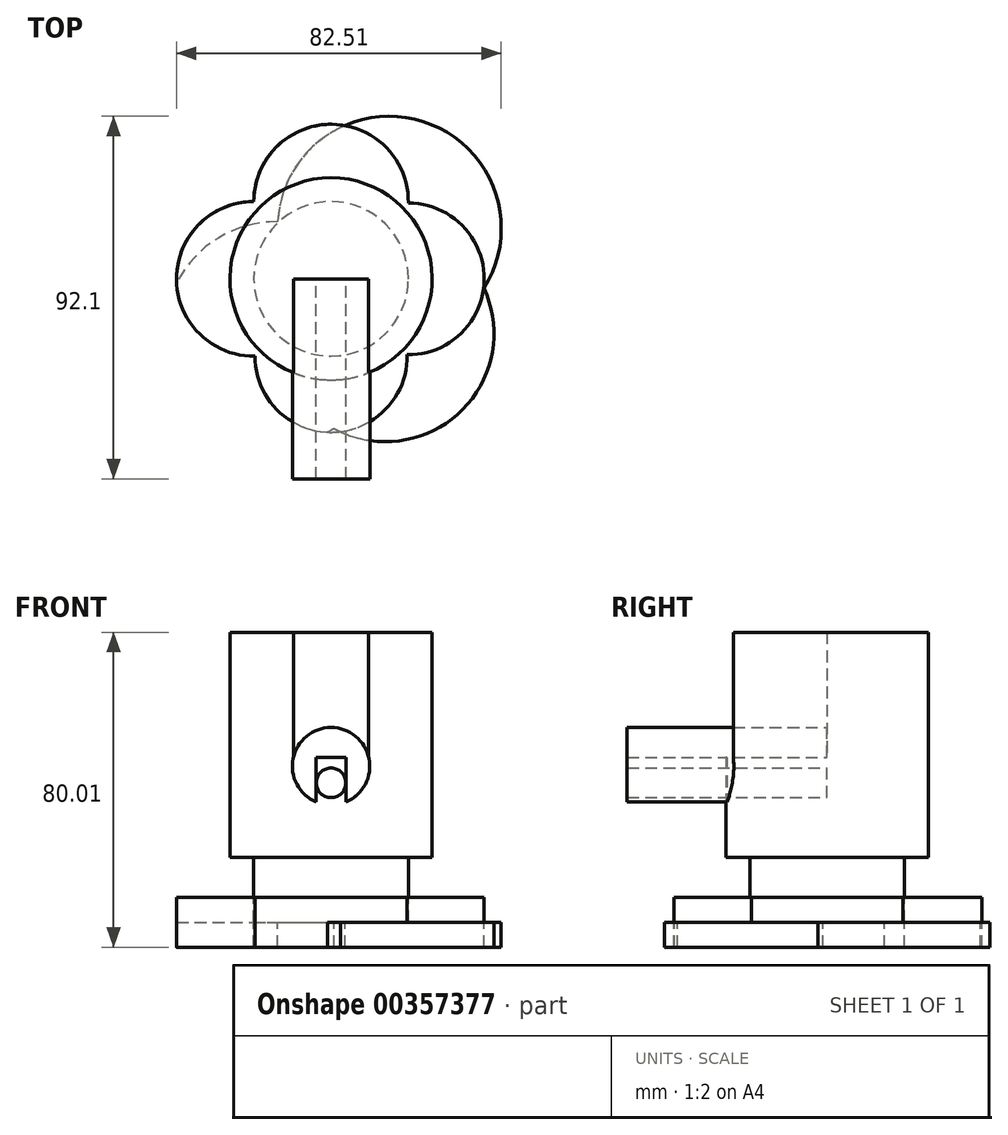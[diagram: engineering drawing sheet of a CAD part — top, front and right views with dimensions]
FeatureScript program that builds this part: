
annotation { "Feature Type Name" : "Feature", "Feature Type Description" : "" }
export const myFeature = defineFeature(function(context is Context, id is Id, definition is map)
    precondition{}
    {
        {
            var Q0;
            Q0=qCreatedBy(makeId("Top.planeOp"),FACE);
            var sketch = newSketch(context, id + "F0", { "sketchPlane" : qUnion([Q0])});
            skCircle(sketch, "E0", {"center": v(0, 0) * mm, "radius": 25.68 * mm});
            skSolve(sketch);
        }
        {
            var Q0;
            Q0=makeQuery(id+"F0.imprint","IMPRINT",FACE,{"disambiguationData":[TD([[makeQuery(id+"F0.imprint","IMPRINT",EDGE,{"derivedFrom":sQuery(id+"F0.wireOp",EDGE,"E0")}),1.0]])]});
            extrude(context, id + "F1", {"entities" : qUnion([Q0]), "depth" : 25.4 * mm, "offsetDistance" : 25.4 * mm});
        }
        {
            var Q0;
            Q0=qCreatedBy(makeId("Front.planeOp"),FACE);
            var sketch = newSketch(context, id + "F2", { "sketchPlane" : qUnion([Q0])});
            skCircle(sketch, "E1", {"center": v(0, 23.13) * mm, "radius": 9.84 * mm});
            skSolve(sketch);
        }
        {
            var Q0;
            Q0=makeQuery(id+"F2.imprint","IMPRINT",FACE,{"disambiguationData":[TD([[makeQuery(id+"F2.imprint","IMPRINT",EDGE,{"derivedFrom":sQuery(id+"F2.wireOp",EDGE,"E1")}),1.0]])]});
            extrude(context, id + "F3", {"entities" : qUnion([Q0]), "operationType" : NewBodyOperationType.ADD, "depth" : 25.4 * mm, "offsetDistance" : 25.4 * mm});
        }
        {
            var Q0;
            Q0=makeQuery(id+"F3.opExtrude","CAP_FACE",FACE,{"disambiguationData":[OSD([sQuery(id+"F2.wireOp",EDGE,"E1")])],"isStart":false});
            extrude(context, id + "F4", {"entities" : qUnion([Q0]), "operationType" : NewBodyOperationType.ADD, "depth" : 25.4 * mm, "offsetDistance" : 25.4 * mm});
        }
        {
            var Q0;
            Q0=qCreatedBy(makeId("Front.planeOp"),FACE);
            var sketch = newSketch(context, id + "F5", { "sketchPlane" : qUnion([Q0])});
            skCircle(sketch, "E2", {"center": v(0, 18.9) * mm, "radius": 3.76 * mm});
            skSolve(sketch);
        }
        {
            var Q0;
            Q0=makeQuery(id+"F5.imprint","IMPRINT",FACE,{"disambiguationData":[TD([[makeQuery(id+"F5.imprint","IMPRINT",EDGE,{"derivedFrom":sQuery(id+"F5.wireOp",EDGE,"E2")}),1.0]])]});
            extrude(context, id + "F6", {"entities" : qUnion([Q0]), "depth" : 50.8 * mm, "offsetDistance" : 25.4 * mm});
        }
        {
            var Q0;
            {var subQ0=sQuery(id+"F0.wireOp",EDGE,"E0");var subQ1=sQuery(id+"F2.wireOp",EDGE,"E1");Q0=makeQuery(id+"F3.boolean.opBoolean","SPLIT",FACE,{"disambiguationData":[TD([makeQuery(id+"F3.opExtrude","SWEPT_FACE",FACE,{"disambiguationData":[OSD([subQ1])]})])],"derivedFrom":makeQuery(id+"F1.opExtrude","CAP_FACE",FACE,{"disambiguationData":[OSD([subQ0])],"isStart":false})});}
            extrude(context, id + "F7", {"entities" : qUnion([Q0]), "operationType" : NewBodyOperationType.ADD, "depth" : 19.05 * mm, "offsetDistance" : 25.4 * mm});
        }
        {
            var Q0;
            Q0=makeQuery(id+"F7.opExtrude","CAP_FACE",FACE,{"disambiguationData":[OSD([sQuery(id+"F0.wireOp",EDGE,"E0")])],"isStart":false});
            extrude(context, id + "F8", {"entities" : qUnion([Q0]), "operationType" : NewBodyOperationType.ADD, "depth" : 12.7 * mm, "offsetDistance" : 25.4 * mm});
        }
        {
            var Q0;
            Q0=qCreatedBy(makeId("Top.planeOp"),FACE);
            var sketch = newSketch(context, id + "F9", { "sketchPlane" : qUnion([Q0])});
            skCircle(sketch, "E3", {"center": v(0, 0) * mm, "radius": 19.63 * mm});
            skSolve(sketch);
        }
        {
            var Q0;
            Q0=makeQuery(id+"F9.imprint","IMPRINT",FACE,{"disambiguationData":[TD([[makeQuery(id+"F9.imprint","IMPRINT",EDGE,{"derivedFrom":sQuery(id+"F9.wireOp",EDGE,"E3")}),1.0]])]});
            extrude(context, id + "F10", {"entities" : qUnion([Q0]), "operationType" : NewBodyOperationType.ADD, "depth" : -10.16 * mm, "offsetDistance" : 25.4 * mm});
        }
        {
            var Q0;
            Q0=makeQuery(id+"F10.opExtrude","CAP_FACE",FACE,{"disambiguationData":[OSD([sQuery(id+"F9.wireOp",EDGE,"E3")])],"isStart":false});
            var sketch = newSketch(context, id + "F11", { "sketchPlane" : qUnion([Q0])});
            skCircle(sketch, "E4", {"center": v(19.63, 0) * mm, "radius": 19.28 * mm});
            skSolve(sketch);
        }
        {
            var Q0;
            {var subQ0=sQuery(id+"F11.wireOp",EDGE,"E4");var subQ1=makeQuery(id+"F10.opExtrude","CAP_EDGE",EDGE,{"disambiguationData":[OSD([sQuery(id+"F9.wireOp",EDGE,"E3")])],"isStart":false});var subQ2=makeQuery(id+"F11.imprint","INTERSECT",VERTEX,{"disambiguationData":[OD(0.0)],"derivedFrom":[subQ1,subQ0]});Q0=makeQuery(id+"F11.imprint","IMPRINT",FACE,{"disambiguationData":[TD([[makeQuery(id+"F11.imprint","IMPRINT",EDGE,{"disambiguationData":[TD([[subQ2,1.0]])],"derivedFrom":subQ0}),1.0]])]});}
            extrude(context, id + "F12", {"entities" : qUnion([Q0]), "depth" : 6.35 * mm, "offsetDistance" : 25.4 * mm});
        }
        {
            var Q0;
            Q0=makeQuery(id+"F10.opExtrude","CAP_FACE",FACE,{"disambiguationData":[OSD([sQuery(id+"F9.wireOp",EDGE,"E3")])],"isStart":false});
            var sketch = newSketch(context, id + "F13", { "sketchPlane" : qUnion([Q0])});
            skCircle(sketch, "E5", {"center": v(0, 19.63) * mm, "radius": 19.35 * mm});
            skSolve(sketch);
        }
        {
            var Q0;
            {var subQ0=sQuery(id+"F13.wireOp",EDGE,"E5");var subQ1=makeQuery(id+"F10.opExtrude","CAP_EDGE",EDGE,{"disambiguationData":[OSD([sQuery(id+"F9.wireOp",EDGE,"E3")])],"isStart":false});var subQ2=makeQuery(id+"F13.imprint","INTERSECT",VERTEX,{"disambiguationData":[OD(0.0)],"derivedFrom":[subQ1,subQ0]});Q0=makeQuery(id+"F13.imprint","IMPRINT",FACE,{"disambiguationData":[TD([[makeQuery(id+"F13.imprint","IMPRINT",EDGE,{"disambiguationData":[TD([[subQ2,1.0]])],"derivedFrom":subQ0}),1.0]])]});}
            extrude(context, id + "F14", {"entities" : qUnion([Q0]), "operationType" : NewBodyOperationType.ADD, "depth" : 6.35 * mm, "offsetDistance" : 25.4 * mm});
        }
        {
            var Q0;
            Q0=makeQuery(id+"F10.opExtrude","CAP_FACE",FACE,{"disambiguationData":[OSD([sQuery(id+"F9.wireOp",EDGE,"E3")])],"isStart":false});
            var sketch = newSketch(context, id + "F15", { "sketchPlane" : qUnion([Q0])});
            skCircle(sketch, "E6", {"center": v(-19.63, 0) * mm, "radius": 19.63 * mm});
            skSolve(sketch);
        }
        {
            var Q0;
            {var subQ0=sQuery(id+"F15.wireOp",EDGE,"E6");var subQ1=makeQuery(id+"F10.opExtrude","CAP_EDGE",EDGE,{"disambiguationData":[OSD([sQuery(id+"F9.wireOp",EDGE,"E3")])],"isStart":false});var subQ2=makeQuery(id+"F15.imprint","INTERSECT",VERTEX,{"disambiguationData":[OD(0.0)],"derivedFrom":[subQ1,subQ0]});Q0=makeQuery(id+"F15.imprint","IMPRINT",FACE,{"disambiguationData":[TD([[makeQuery(id+"F15.imprint","IMPRINT",EDGE,{"disambiguationData":[TD([[subQ2,-1.0]])],"derivedFrom":subQ0}),1.0]])]});}
            extrude(context, id + "F16", {"entities" : qUnion([Q0]), "operationType" : NewBodyOperationType.ADD, "depth" : 6.35 * mm, "offsetDistance" : 25.4 * mm});
        }
        {
            var Q0;
            Q0=makeQuery(id+"F10.opExtrude","CAP_FACE",FACE,{"disambiguationData":[OSD([sQuery(id+"F9.wireOp",EDGE,"E3")])],"isStart":false});
            var sketch = newSketch(context, id + "F17", { "sketchPlane" : qUnion([Q0])});
            skCircle(sketch, "E7", {"center": v(0, -19.63) * mm, "radius": 19.63 * mm});
            skSolve(sketch);
        }
        {
            var Q0;
            {var subQ0=sQuery(id+"F17.wireOp",EDGE,"E7");var subQ1=makeQuery(id+"F10.opExtrude","CAP_EDGE",EDGE,{"disambiguationData":[OSD([sQuery(id+"F9.wireOp",EDGE,"E3")])],"isStart":false});var subQ2=makeQuery(id+"F17.imprint","INTERSECT",VERTEX,{"disambiguationData":[OD(0.0)],"derivedFrom":[subQ1,subQ0]});Q0=makeQuery(id+"F17.imprint","IMPRINT",FACE,{"disambiguationData":[TD([[makeQuery(id+"F17.imprint","IMPRINT",EDGE,{"disambiguationData":[TD([[subQ2,-1.0]])],"derivedFrom":subQ0}),1.0]])]});}
            extrude(context, id + "F18", {"entities" : qUnion([Q0]), "operationType" : NewBodyOperationType.ADD, "depth" : 6.35 * mm, "offsetDistance" : 25.4 * mm});
        }
        {
            var Q0;
            Q0=makeQuery(id+"F10.opExtrude","CAP_FACE",FACE,{"disambiguationData":[OSD([sQuery(id+"F9.wireOp",EDGE,"E3")])],"isStart":false});
            extrude(context, id + "F19", {"entities" : qUnion([Q0]), "depth" : 6.35 * mm, "offsetDistance" : 25.4 * mm});
        }
        {
            var Q0;
            Q0=makeQuery(id+"F19.opExtrude","CAP_FACE",FACE,{"disambiguationData":[OSD([sQuery(id+"F9.wireOp",EDGE,"E3")])],"isStart":false});
            var sketch = newSketch(context, id + "F20", { "sketchPlane" : qUnion([Q0])});
            skCircle(sketch, "E8", {"center": v(13.88, 13.88) * mm, "radius": 27.49 * mm});
            skSolve(sketch);
        }
        {
            var Q0;
            {var subQ0=sQuery(id+"F20.wireOp",EDGE,"E8");var subQ1=makeQuery(id+"F19.opExtrude","CAP_EDGE",EDGE,{"disambiguationData":[OSD([sQuery(id+"F9.wireOp",EDGE,"E3")])],"isStart":false});var subQ2=makeQuery(id+"F20.imprint","INTERSECT",VERTEX,{"disambiguationData":[OD(0.0)],"derivedFrom":[subQ1,subQ0]});Q0=makeQuery(id+"F20.imprint","IMPRINT",FACE,{"disambiguationData":[TD([[makeQuery(id+"F20.imprint","IMPRINT",EDGE,{"disambiguationData":[TD([[subQ2,1.0]])],"derivedFrom":subQ0}),1.0]])]});}
            extrude(context, id + "F21", {"entities" : qUnion([Q0]), "operationType" : NewBodyOperationType.ADD, "depth" : 6.35 * mm, "offsetDistance" : 25.4 * mm});
        }
        {
            var Q0;
            Q0=makeQuery(id+"F19.opExtrude","CAP_FACE",FACE,{"disambiguationData":[OSD([sQuery(id+"F9.wireOp",EDGE,"E3")])],"isStart":false});
            var sketch = newSketch(context, id + "F22", { "sketchPlane" : qUnion([Q0])});
            skCircle(sketch, "E9", {"center": v(-13.95, 13.81) * mm, "radius": 28.31 * mm});
            skSolve(sketch);
        }
        {
            var Q0;
            {var subQ0=sQuery(id+"F22.wireOp",EDGE,"E9");var subQ1=makeQuery(id+"F19.opExtrude","CAP_EDGE",EDGE,{"disambiguationData":[OSD([sQuery(id+"F9.wireOp",EDGE,"E3")])],"isStart":false});var subQ2=makeQuery(id+"F22.imprint","INTERSECT",VERTEX,{"disambiguationData":[OD(0.0)],"derivedFrom":[subQ1,subQ0]});Q0=makeQuery(id+"F22.imprint","IMPRINT",FACE,{"disambiguationData":[TD([[makeQuery(id+"F22.imprint","IMPRINT",EDGE,{"disambiguationData":[TD([[subQ2,1.0]])],"derivedFrom":subQ0}),1.0]])]});}
            extrude(context, id + "F23", {"entities" : qUnion([Q0]), "operationType" : NewBodyOperationType.ADD, "depth" : 6.35 * mm, "offsetDistance" : 25.4 * mm});
        }
        {
            var Q0;
            Q0=makeQuery(id+"F19.opExtrude","CAP_FACE",FACE,{"disambiguationData":[OSD([sQuery(id+"F9.wireOp",EDGE,"E3")])],"isStart":false});
            var sketch = newSketch(context, id + "F24", { "sketchPlane" : qUnion([Q0])});
            skCircle(sketch, "E10", {"center": v(-13.7, -14.06) * mm, "radius": 28.91 * mm});
            skSolve(sketch);
        }
        {
            var Q0;
            {var subQ0=sQuery(id+"F24.wireOp",EDGE,"E10");var subQ1=makeQuery(id+"F19.opExtrude","CAP_EDGE",EDGE,{"disambiguationData":[OSD([sQuery(id+"F9.wireOp",EDGE,"E3")])],"isStart":false});var subQ2=makeQuery(id+"F24.imprint","INTERSECT",VERTEX,{"disambiguationData":[OD(0.0)],"derivedFrom":[subQ1,subQ0]});Q0=makeQuery(id+"F24.imprint","IMPRINT",FACE,{"disambiguationData":[TD([[makeQuery(id+"F24.imprint","IMPRINT",EDGE,{"disambiguationData":[TD([[subQ2,-1.0]])],"derivedFrom":subQ0}),1.0]])]});}
            extrude(context, id + "F25", {"entities" : qUnion([Q0]), "operationType" : NewBodyOperationType.ADD, "depth" : 6.35 * mm, "offsetDistance" : 25.4 * mm});
        }
        {
            var Q0;
            Q0=makeQuery(id+"F19.opExtrude","CAP_FACE",FACE,{"disambiguationData":[OSD([sQuery(id+"F9.wireOp",EDGE,"E3")])],"isStart":false});
            var sketch = newSketch(context, id + "F26", { "sketchPlane" : qUnion([Q0])});
            skCircle(sketch, "E11", {"center": v(14.82, -12.88) * mm, "radius": 28.42 * mm});
            skSolve(sketch);
        }
        {
            var Q0;
            {var subQ0=sQuery(id+"F26.wireOp",EDGE,"E11");var subQ1=makeQuery(id+"F19.opExtrude","CAP_EDGE",EDGE,{"disambiguationData":[OSD([sQuery(id+"F9.wireOp",EDGE,"E3")])],"isStart":false});var subQ2=makeQuery(id+"F26.imprint","INTERSECT",VERTEX,{"disambiguationData":[OD(0.0)],"derivedFrom":[subQ1,subQ0]});Q0=makeQuery(id+"F26.imprint","IMPRINT",FACE,{"disambiguationData":[TD([[makeQuery(id+"F26.imprint","IMPRINT",EDGE,{"disambiguationData":[TD([[subQ2,-1.0]])],"derivedFrom":subQ0}),1.0]])]});}
            extrude(context, id + "F27", {"entities" : qUnion([Q0]), "operationType" : NewBodyOperationType.ADD, "depth" : 6.35 * mm, "offsetDistance" : 25.4 * mm});
        }
        {
            var Q0;
            Q0=makeQuery(id+"F19.opExtrude","CAP_FACE",FACE,{"disambiguationData":[OSD([sQuery(id+"F9.wireOp",EDGE,"E3")])],"isStart":false});
            extrude(context, id + "F28", {"entities" : qUnion([Q0]), "depth" : 6.35 * mm, "offsetDistance" : 25.4 * mm});
        }
    });
